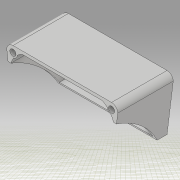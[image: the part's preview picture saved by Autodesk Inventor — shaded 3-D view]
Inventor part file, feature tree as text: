
AUTODESK INVENTOR PART (.ipt)
format: ipt  version: 2018 (Build 220112000, 112)  size: 227,840 bytes
history: native  units: in
note: dims shown in document units (in); Inventor stores cm internally (conversion verified against a paired STEP export)
features: extrude x7, sketch x7, projected_geometry x3, mirror x1
ambient origin geometry x8: Origin, YZ Plane, XZ Plane, XY Plane, X Axis, Y Axis, Z Axis, Center Point
bodies: Solid1 (feature_tree)
feature tree (18):
  extrude  "Extrusion1"  Depth=2.0in
  extrude  "Extrusion2"  Depth=0.25in
  mirror  "Mirror1"
  extrude  "Extrusion3"  Depth=0.5in
  extrude  "Extrusion4"  Depth=0.12in
  extrude  "Extrusion5"  Depth=0.35in
  extrude  "Extrusion6"  Depth=1.0in TaperAngle=0.0deg
  extrude  "Extrusion7"  Depth=2.0in TaperAngle=0.0deg
  sketch  "Sketch1"  dims[d0=4.0in d1=2.0in]
  sketch  "Sketch2"  dims[d2=0.25in d3=0.25in]
  projected_geometry  "Projected Loop1"
  sketch  "Sketch3"  dims[d4=0.5in d5=0.5in]
  sketch  "Sketch5"  dims[d6=0.25in d7=0.0in d8=0.12in]
  projected_geometry  "Projected Loop3"
  sketch  "Sketch6"  dims[d9=1.0in d10=0.0in d11=0.35in]
  projected_geometry  "Projected Loop4"
  sketch  "Sketch7"  dims[d12=0.35in d13=1.0in d14=0.0in]
  sketch  "Sketch8"  dims[d15=2.0in d16=0.0in d18=2.0in d19=0.0in d20=0.4in d21=3.5in d22=10.0in d23=0.0in d24=11.0in d25=0.0in]
